# Revit family: ASH_ArmitageShanks_CounterTopWashBasins_Sandringham21-50cmSemiCTop
name_source: partatom
category: Plumbing Fixtures
revit_build: Autodesk Revit MEP 2012 (Build: 20110309_2315(x64)
units: mm (PartAtom-declared; Revit-internal decimal feet)

## types (3) — shared parameters
Accessories = www.idealspec.co.uk
AreaUnits = millimeters
Assembly Code = C1030200
AssetType = Fixed
BasinMaterial = ASH_ArmitageShanks _Sanitaryware_White5_Render
Brand = Armitage Shanks
Category = SanitaryTerminal_WASHHANDBASIN_UK
Color = White
ConnectionType = Plumbing
Default Elevation = 1219 mm
DrainSize = 32 mm  [stored 0.104987 ft]
DurationUnit = year
ECA = No
ExpectedLife = 30
Finish = White
IfcExportAs = IfcSanitaryTerminalType
IfcExportType = WASHHANDBASIN
InstallationInstructions = www.idealspec.co.uk/resources.html
LinearUnits = millimeters
ManufacturerURL = www.idealspec.co.uk
Material = Vitreous china
NBSDescription = Counter top wash basins
NBSReference = 45-35-70/360
NettWeight = 13.39 Kg
NominalDepth = 444 mm
NominalHeight = 185 mm
NominalLength = 444 mm
NominalWidth = 500 mm
Shape = Sculptured
Size = 500 x 445 x 185 mm
Space = Internal
SpareParts = www.fastpart-spares.co.uk
URL = www.idealspec.co.uk
Uniclass2 = Pr_40_20_96_18
Version = 1
VolumeUnits = Litres
WRAS = No
WarrantyDescription = Manufacturers warranty
WarrantyDurationParts = 99
WarrantyDurationUnit = year
WashHandBasinMounting = CounterTop
WashHandBasinType = HANDRINSE
WaterEfficientProduct = No
zero-valued in all types: CWFU, HWFU, WFU

## per-type parameters (varying)
| type | BIMObjectName | Description | E895801-1Th | E895901-2Th | Features | Model | ModelNumber | ModelReference | Name | ProductInformation |
| E895801 - Sandringham 21 50cm semi-countertop washbasin, 1 taphole with overflow no chainstay hole | ASH_ArmitageShanks_CounterTopWashBasins_Sandringham21_E8958 | Sandringham 21 50 cm semi-countertop washbasin, 1 taphole with overflow no chainstay hole | Yes | No | 50 cm semi-countertop washbasin, 1 taphole with overflow no chainstay hole | E895801 | E895801 | Sandringham 21 50 cm semi-countertop washbasin, 1 taphole with overflow no chainstay hole | CounterTopWashBasins_Sandringham21_E8958_ArmitageShanks | www.idealspec.co.uk/assets/datasheet/E895801 |
| E895901 - Sandringham 21 semi-countertop washbasin 50cm, 2 tapholes with overflow and chainstay hole | ASH_ArmitageShanks_CounterTopWashBasins_Sandringham21_E8959 | Sandringham 21 semi-countertop washbasin 50 cm, 2 tapholes with overflow and chainstay hole | No | Yes | 50 cm semi-countertop washbasin, 2 tapholes with overflow and chainstay hole | E895901 | E895901 | Sandringham 21 semi-countertop washbasin 50 cm, 2 tapholes with overflow and chainstay hole | CounterTopWashBasins_Sandringham21_E8959_ArmitageShanks | www.idealspec.co.uk/assets/datasheet/E895901 |
| E896101 - Sandringham 21 semi-countertop washbasin 50cm, 2 tapholes with overflow no chainstay hole | ASH_ArmitageShanks_CounterTopWashBasins_Sandringham21_E8961 | Sandringham 21 semi-countertop washbasin 50 cm, 2 tapholes with overflow no chainstay hole | No | Yes | 50 cm semi-countertop washbasin , 2 tapholes with overflow no chainstay hole | E896101 | E896101 | Sandringham 21 semi-countertop washbasin 50 cm, 2 tapholes with overflow no chainstay hole | CounterTopWashBasins_Sandringham21_E8961_ArmitageShanks | www.idealspec.co.uk/assets/datasheet/E896101 |

note: [stored X ft] marks values corroborated as IEEE doubles in the binary element streams (Revit-internal decimal feet)

## geometry (parser evidence)
native form markers: Sweep x9
no freeform markers — native parametric forms only
